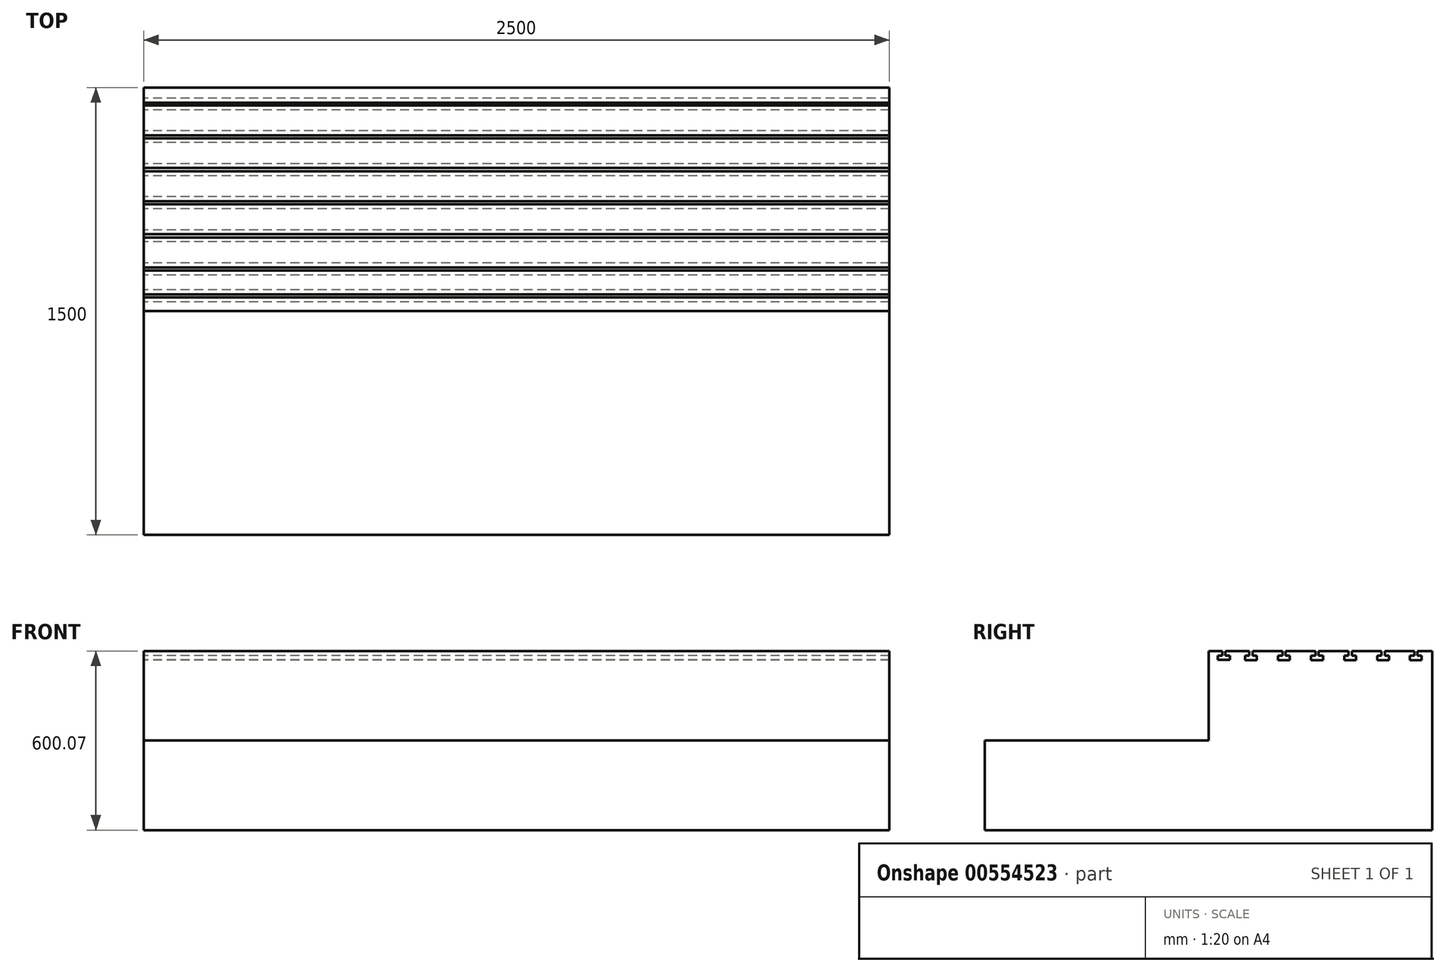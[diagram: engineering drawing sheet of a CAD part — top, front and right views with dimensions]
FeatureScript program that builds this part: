
annotation { "Feature Type Name" : "Feature", "Feature Type Description" : "" }
export const myFeature = defineFeature(function(context is Context, id is Id, definition is map)
    precondition{}
    {
        {
            var Q0;
            Q0=qCreatedBy(makeId("Right.planeOp"),FACE);
            var sketch = newSketch(context, id + "F0", { "sketchPlane" : qUnion([Q0])});
            skLineSegment(sketch, "E0", {"start": v(0, 0) * mm, "end": v(0, 600) * mm});
            skLineSegment(sketch, "E1", {"start": v(0, 0) * mm, "end": v(-1500, 0) * mm});
            skLineSegment(sketch, "E2", {"start": v(-1500, 0) * mm, "end": v(-1500, 299.93) * mm});
            skLineSegment(sketch, "E3", {"start": v(-1500, 299.93) * mm, "end": v(-750, 299.93) * mm});
            skLineSegment(sketch, "E4", {"start": v(-750, 299.93) * mm, "end": v(-750, 600) * mm});
            skLineSegment(sketch, "E5", {"start": v(0, 600) * mm, "end": v(-50.27, 600) * mm});
            skLineSegment(sketch, "E6", {"start": v(-50.27, 600) * mm, "end": v(-50.27, 585.11) * mm});
            skLineSegment(sketch, "E7", {"start": v(-50.27, 585.11) * mm, "end": v(-35.4, 585.11) * mm});
            skLineSegment(sketch, "E8", {"start": v(-35.4, 585.11) * mm, "end": v(-35.4, 570.24) * mm});
            skLineSegment(sketch, "E9", {"start": v(-35.4, 570.24) * mm, "end": v(-75.22, 570.24) * mm});
            skLineSegment(sketch, "E10", {"start": v(-75.22, 570.24) * mm, "end": v(-75.22, 585.45) * mm});
            skLineSegment(sketch, "E11", {"start": v(-75.22, 585.45) * mm, "end": v(-59.92, 585.45) * mm});
            skLineSegment(sketch, "E12", {"start": v(-59.92, 585.45) * mm, "end": v(-59.92, 600.07) * mm});
            skLineSegment(sketch, "E13", {"start": v(-59.92, 600.07) * mm, "end": v(-159.7, 600.07) * mm});
            skLineSegment(sketch, "E14", {"start": v(-159.7, 600.07) * mm, "end": v(-159.7, 584.93) * mm});
            skLineSegment(sketch, "E15", {"start": v(-159.7, 584.93) * mm, "end": v(-144.55, 584.93) * mm});
            skLineSegment(sketch, "E16", {"start": v(-144.55, 584.93) * mm, "end": v(-144.55, 570.24) * mm});
            skLineSegment(sketch, "E17", {"start": v(-144.55, 570.24) * mm, "end": v(-184.8, 570.24) * mm});
            skLineSegment(sketch, "E18", {"start": v(-184.8, 570.24) * mm, "end": v(-184.8, 584.93) * mm});
            skLineSegment(sketch, "E19", {"start": v(-184.8, 584.93) * mm, "end": v(-170.15, 584.93) * mm});
            skLineSegment(sketch, "E20", {"start": v(-170.15, 584.93) * mm, "end": v(-170.15, 600.07) * mm});
            skLineSegment(sketch, "E21", {"start": v(-170.15, 600.07) * mm, "end": v(-269.69, 600.07) * mm});
            skLineSegment(sketch, "E22", {"start": v(-269.69, 600.07) * mm, "end": v(-269.69, 584.93) * mm});
            skLineSegment(sketch, "E23", {"start": v(-269.69, 584.93) * mm, "end": v(-255.1, 584.93) * mm});
            skLineSegment(sketch, "E24", {"start": v(-255.1, 584.93) * mm, "end": v(-255.1, 570.24) * mm});
            skLineSegment(sketch, "E25", {"start": v(-255.1, 570.24) * mm, "end": v(-295.56, 570.24) * mm});
            skLineSegment(sketch, "E26", {"start": v(-295.56, 570.24) * mm, "end": v(-295.56, 584.93) * mm});
            skLineSegment(sketch, "E27", {"start": v(-295.56, 584.93) * mm, "end": v(-280.84, 584.93) * mm});
            skLineSegment(sketch, "E28", {"start": v(-280.84, 584.93) * mm, "end": v(-280.84, 600.07) * mm});
            skLineSegment(sketch, "E29", {"start": v(-280.84, 600.07) * mm, "end": v(-380.71, 600.07) * mm});
            skLineSegment(sketch, "E30", {"start": v(-380.71, 600.07) * mm, "end": v(-380.71, 584.93) * mm});
            skLineSegment(sketch, "E31", {"start": v(-380.71, 584.93) * mm, "end": v(-365.76, 584.93) * mm});
            skLineSegment(sketch, "E32", {"start": v(-365.76, 584.93) * mm, "end": v(-365.76, 570.24) * mm});
            skLineSegment(sketch, "E33", {"start": v(-365.76, 570.24) * mm, "end": v(-406.2, 570.24) * mm});
            skLineSegment(sketch, "E34", {"start": v(-406.2, 570.24) * mm, "end": v(-406.2, 584.93) * mm});
            skLineSegment(sketch, "E35", {"start": v(-406.2, 584.93) * mm, "end": v(-391.43, 584.93) * mm});
            skLineSegment(sketch, "E36", {"start": v(-391.43, 584.93) * mm, "end": v(-391.43, 600.07) * mm});
            skLineSegment(sketch, "E37", {"start": v(-391.43, 600.07) * mm, "end": v(-491.9, 600.07) * mm});
            skLineSegment(sketch, "E38", {"start": v(-491.9, 600.07) * mm, "end": v(-491.9, 584.93) * mm});
            skLineSegment(sketch, "E39", {"start": v(-491.9, 584.93) * mm, "end": v(-477.34, 584.93) * mm});
            skLineSegment(sketch, "E40", {"start": v(-477.34, 584.93) * mm, "end": v(-477.34, 570.24) * mm});
            skLineSegment(sketch, "E41", {"start": v(-477.34, 570.24) * mm, "end": v(-517.56, 570.24) * mm});
            skLineSegment(sketch, "E42", {"start": v(-517.56, 570.24) * mm, "end": v(-517.56, 584.93) * mm});
            skLineSegment(sketch, "E43", {"start": v(-517.56, 584.93) * mm, "end": v(-502.48, 584.93) * mm});
            skLineSegment(sketch, "E44", {"start": v(-502.48, 584.93) * mm, "end": v(-502.48, 600.07) * mm});
            skLineSegment(sketch, "E45", {"start": v(-502.48, 600.07) * mm, "end": v(-602.94, 600.07) * mm});
            skLineSegment(sketch, "E46", {"start": v(-602.94, 600.07) * mm, "end": v(-602.94, 584.93) * mm});
            skLineSegment(sketch, "E47", {"start": v(-602.94, 584.93) * mm, "end": v(-588.39, 584.93) * mm});
            skLineSegment(sketch, "E48", {"start": v(-588.39, 584.93) * mm, "end": v(-588.39, 570.24) * mm});
            skLineSegment(sketch, "E49", {"start": v(-588.39, 570.24) * mm, "end": v(-628.2, 570.24) * mm});
            skLineSegment(sketch, "E50", {"start": v(-628.2, 570.24) * mm, "end": v(-628.2, 584.93) * mm});
            skLineSegment(sketch, "E51", {"start": v(-628.2, 584.93) * mm, "end": v(-613.65, 584.93) * mm});
            skLineSegment(sketch, "E52", {"start": v(-613.65, 584.93) * mm, "end": v(-613.65, 600.07) * mm});
            skLineSegment(sketch, "E53", {"start": v(-613.65, 600.07) * mm, "end": v(-694.04, 600.07) * mm});
            skLineSegment(sketch, "E54", {"start": v(-694.04, 600.07) * mm, "end": v(-694.04, 585.47) * mm});
            skLineSegment(sketch, "E55", {"start": v(-694.04, 585.47) * mm, "end": v(-678.9, 585.47) * mm});
            skLineSegment(sketch, "E56", {"start": v(-678.9, 585.47) * mm, "end": v(-678.9, 570.85) * mm});
            skLineSegment(sketch, "E57", {"start": v(-678.9, 570.85) * mm, "end": v(-719.36, 570.85) * mm});
            skLineSegment(sketch, "E58", {"start": v(-719.36, 570.85) * mm, "end": v(-719.36, 585.47) * mm});
            skLineSegment(sketch, "E59", {"start": v(-719.36, 585.47) * mm, "end": v(-704.23, 585.47) * mm});
            skLineSegment(sketch, "E60", {"start": v(-704.23, 585.47) * mm, "end": v(-704.23, 600.07) * mm});
            skLineSegment(sketch, "E61", {"start": v(-704.23, 600.07) * mm, "end": v(-750, 600) * mm});
            skSolve(sketch);
        }
        {
            var Q0;
            Q0=makeQuery(id+"F0.imprint","IMPRINT",FACE,{"disambiguationData":[TD([[makeQuery(id+"F0.imprint","IMPRINT",EDGE,{"derivedFrom":sQuery(id+"F0.wireOp",EDGE,"E0")}),1.0]])]});
            extrude(context, id + "F1", {"entities" : qUnion([Q0]), "depth" : 2500 * mm, "offsetDistance" : 25 * mm});
        }
    });
